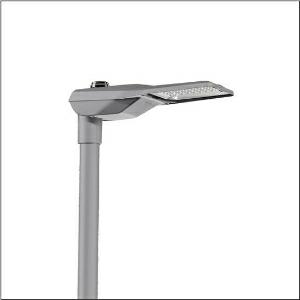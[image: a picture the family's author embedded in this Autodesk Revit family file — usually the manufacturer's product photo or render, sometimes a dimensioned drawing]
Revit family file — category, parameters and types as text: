
# Revit family: streetlight_sl_21_mini___p1_0a_5xe6a47n08gb_c068
name_source: partatom
category: Lighting Fixtures
units: mm (PartAtom-declared; Revit-internal decimal feet)

## family parameters
Cut with Voids When Loaded = No
Host = Face
Light Source = No
Part Type = Normal
Room Calculation Point = No
Round Connector Dimension = Use Diameter
Shared = No

## types (1)
- --- (1 x LED, 6180 lm, 40.4 W, 4000K)
    Apparent Load = 40 VA
    CIE Flux Codes = 21 50 90 100 100
    Color Rendering = 70
    Color Temperature = 4000K
    Default Elevation = 1800 mm
    Description = Streetlight SL 21 mini, mast luminaire, primary light control with lens, of PMMA, primary optical cover: cover, of toughened safety glass, transparent, light distribution: P1.0a, light emission: direct distribution, primary light characteristic: asymmetric, installation type: side-entry, LED, 3G 1.5mm², High Power LED, rated luminous flux: 6.180lm, luminous efficacy: 153lm/W, light colour: 740, colour temperature: 4000K, control gear: NEMA (7pin), control: overheat protection, pre-setting: linear dimming characteristic, constant luminous flux control, time-dependent luminous flux control, flexible luminous flux parameterisation, mains connection: 230..240V, AC, 50/60Hz, connection cable pre-assembled, cable length: 8,5m, wiring characteristics: H07RN-F, start of lifetime: 40W, end of service life: 41W, reduction: 19W, luminaire housing, of diecast aluminium (EN AC-44300), powder-coated, SITECO metallic grey (DB 702S), corrosivity category C5 high according to DIN EN ISO 12944, multi-level sealing system, sealing non-destructively replaceable, inclination adjustable: 0°, 5°, 10°, 15°, length: 628mm, width: 235mm, height: 110mm, spigot size: 42mm (side-entry), mounting height: 4..8m, protection rating (complete): IP66, insulation class (complete): insulation class I (protective earthing), certification: CE, ENEC, ENEC+, VDE, impact resistance: IK10, permissible operating ambient temperature for outdoor applications: -40..+50°C, standard-compliant lighting for roads and squares, packaging unit: 1 piece

Light Distribution: P1.0a
    Height = 110 mm
    Lamp = 1 x LED
    Lamp Light Flux = 6180 lm
    Lamp Power = 40.4 W
    Lamp count = 1
    Length = 625 mm
    Luminous efficacy = 153 lm/W
    Manufacturer = Siteco
    ModVariant = No
    Model = 5XE6A47N08GB
    Number of Poles = 1
    OnlyDefault = Yes
    Power Factor = 1
    Product Name = Streetlight SL 21 mini | P1.0a
    Product group = mast luminaire | pylon top
    ProductGroupID = 6100
    Protection Class = Protection class I
    Protection Degree = IP 66
    RLX_Detail_Level = 1
    RLX_Emergency_Light_Flux = 0 lm
    RLX_Emergency_Type = 0
    RLX_Emergency_Type_DB = No
    RlxData = <blob elided: 36997 chars, md5=5864cedd>
    Socket = socket
    Standby Power = 0 W
    System Light Flux = 6180 lm
    System Power = 40 W
    Type Comments = factory setting: luminous flux: 100 % | dim-lin: 254 | 812 mA
    Type Image = l_1294379.jpg
    URL = http://relux.com
    VarID = @adj_134135
    Voltage = 0 V
    Weight = 0.00 kg
    Width = 234 mm

## geometry (parser evidence)
native form markers: Blend x4, Sweep x10
no freeform markers — native parametric forms only
